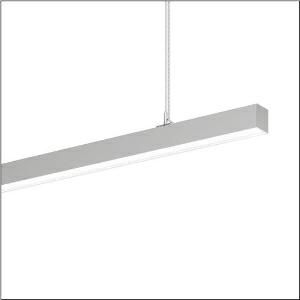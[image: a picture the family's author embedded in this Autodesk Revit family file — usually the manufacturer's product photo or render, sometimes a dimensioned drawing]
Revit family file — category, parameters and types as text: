
# Revit family: silica_r__21_51mx30tat4s_875d
name_source: partatom
category: Lighting Fixtures
units: mm (PartAtom-declared; Revit-internal decimal feet)

## family parameters
Cut with Voids When Loaded = No
Host = Face
Light Source = No
Part Type = Normal
Room Calculation Point = No
Round Connector Dimension = Use Diameter
Shared = No

## types (1)
- --- (1 x LED, 4120 lm, 33.8 W, 6500K)
    Apparent Load = 34 VA
    CIE Flux Codes = 47 79 96 58 100
    Color Rendering = 80
    Color Temperature = 6500K
    Default Elevation = 1800 mm
    Description = Silica® 21, office luminaire, primary optical cover: cover, of PMMA, opal, light emission: direct/indirect distribution, primary light characteristic: symmetric, installation type: suspended mounting, LED, rated luminous flux: 4.120lm, luminous efficacy: 116lm/W, light colour: 8tw, colour temperature: 2700..6500K, control gear: ECG DALI, with terminal, 3+2-pole, max. 2.5mm², mains connection: 220..240V, AC, 50/60Hz, rated input power: 35.5W, luminaire housing, of aluminium, metallic grey (RAL 9006), length: 1.204mm, width: 53mm, height: 53mm, protection rating (complete): IP20, insulation class (complete): insulation class I (protective earthing), certification: CE, permissible operating ambient temperature: 0..+35°C, standard: EN 50419, packaging unit: 1 piece
    Height = 53 mm
    Lamp = 1 x LED
    Lamp Light Flux = 4120 lm
    Lamp Power = 33.8 W
    Lamp count = 1
    Length = 1204 mm
    Luminous efficacy = 122 lm/W
    Manufacturer = Siteco
    ModVariant = No
    Model = 51MX30TAT4S
    Mounting Place = Ceiling
    Mounting Type = Pendant
    Number of Poles = 1
    OnlyDefault = Yes
    Power Factor = 1
    Product Name = Silica® 21
    Product group = office luminaire | ceiling pendant
    ProductGroupID = 902
    Protection Class = Protection class I
    Protection Degree = IP 20
    RLX_Detail_Level = 1
    RLX_Emergency_Light_Flux = 0 lm
    RLX_Emergency_Type = 0
    RLX_Emergency_Type_DB = No
    RlxData = <blob elided: 20117 chars, md5=7013e792>
    Socket = socket
    Standby Power = 0 W
    System Light Flux = 4120 lm
    System Power = 34 W
    Type Comments = individual setting
    Type Image = l_1335864.jpg
    URL = http://relux.com
    VarID = @adj_109423
    Voltage = 0 V
    Weight = 0.00 kg
    Width = 53 mm

## geometry (parser evidence)
native form markers: Blend x4, Sweep x13
no freeform markers — native parametric forms only
